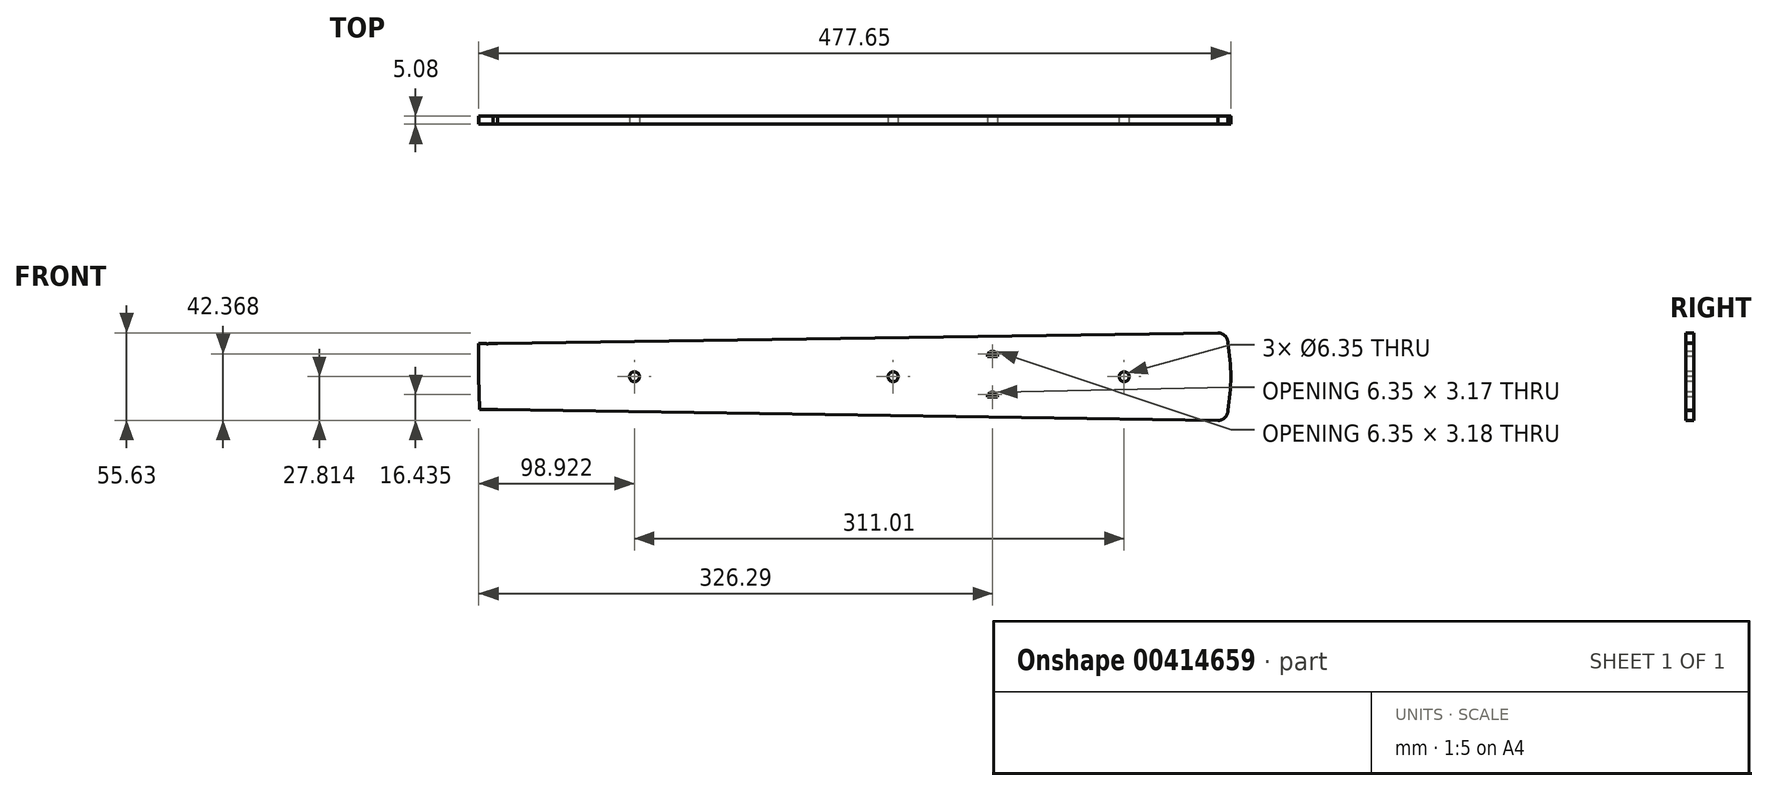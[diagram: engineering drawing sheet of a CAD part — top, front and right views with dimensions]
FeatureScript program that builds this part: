
annotation { "Feature Type Name" : "Feature", "Feature Type Description" : "" }
export const myFeature = defineFeature(function(context is Context, id is Id, definition is map)
    precondition{}
    {
        {
            var Q0;
            Q0=qCreatedBy(makeId("Front.planeOp"),FACE);
            var sketch = newSketch(context, id + "F0", { "sketchPlane" : qUnion([Q0])});
            skLineSegment(sketch, "E0", {"start": v(-164.23, 27.6) * mm, "end": v(293.18, 27.6) * mm});
            skLineSegment(sketch, "E1", {"start": v(-164.23, 48.56) * mm, "end": v(-164.23, 6.65) * mm});
            skLineSegment(sketch, "E2", {"start": v(-164.23, 6.65) * mm, "end": v(293.18, -0.2) * mm});
            skLineSegment(sketch, "E3", {"start": v(293.18, -0.2) * mm, "end": v(293.18, 55.42) * mm});
            skLineSegment(sketch, "E4", {"start": v(293.18, 55.42) * mm, "end": v(-164.23, 48.56) * mm});
            skArc(sketch, "E5", {"start": v(293.18, -0.2) * mm, "mid": v(297.7, 1.67) * mm, "end": v(299.53, 6.2) * mm});
            skArc(sketch, "E6", {"start": v(299.53, 49) * mm, "mid": v(297.7, 53.53) * mm, "end": v(293.18, 55.42) * mm});
            skArc(sketch, "E7", {"start": v(299.53, 6.2) * mm, "mid": v(301.35, 27.6) * mm, "end": v(299.53, 49) * mm});
            skLineSegment(sketch, "E8.MirrorCS", {"start": v(-167.3, 6.65) * mm, "end": v(-167.3, 48.56) * mm});
            skLineSegment(sketch, "E9.MirrorCS", {"start": v(-175.73, 6.7) * mm, "end": v(-167.3, 6.65) * mm});
            skFitSpline(sketch, "E10.MirrorCS", {"points": [v(-167.3, 48.56) * mm, v(-173.6, 48.56) * mm, v(-180.07, 49.1) * mm, v(-184.37, 49.72) * mm, v(-187.7, 50.38) * mm, v(-189.62, 50.86) * mm, v(-191.82, 51.86) * mm, v(-194.74, 53.34) * mm, v(-198.5, 55.52) * mm, v(-201.03, 57.21) * mm, v(-203.1, 58.73) * mm, v(-204.96, 60.23) * mm, v(-206.37, 61.4) * mm, v(-207.64, 62.55) * mm, v(-209.47, 64.33) * mm, v(-210.92, 65.83) * mm, v(-212, 66.98) * mm, v(-213.97, 69.33) * mm, v(-215.82, 71.75) * mm, v(-217.07, 73.74) * mm], "startDerivative": vector(-80.82, -1.68) * mm, "endDerivative": vector(-28.5, 40.15) * mm});
            skLineSegment(sketch, "E11", {"start": v(-167.3, 48.56) * mm, "end": v(-164.23, 48.56) * mm});
            skLineSegment(sketch, "E12", {"start": v(-164.23, 27.6) * mm, "end": v(-176.3, 27.6) * mm});
            skPoint(sketch, "E13", {"position": v(-127.89, 27.6) * mm});
            skPoint(sketch, "E14", {"position": v(-93.57, 27.6) * mm});
            skPoint(sketch, "E15", {"position": v(-61.19, 27.6) * mm});
            skPoint(sketch, "E16", {"position": v(-30.6, 27.6) * mm});
            skLineSegment(sketch, "E17", {"start": v(-127.89, 49.1) * mm, "end": v(-127.89, 6.1) * mm});
            skLineSegment(sketch, "E18", {"start": v(-93.57, 49.62) * mm, "end": v(-93.57, 27.6) * mm});
            skLineSegment(sketch, "E19", {"start": v(-61.19, 5.1) * mm, "end": v(-61.19, 50.1) * mm});
            skLineSegment(sketch, "E20", {"start": v(-30.6, 50.56) * mm, "end": v(-30.6, 4.65) * mm});
            skPoint(sketch, "E21", {"position": v(-1.75, 27.6) * mm});
            skPoint(sketch, "E22", {"position": v(25.48, 27.6) * mm});
            skPoint(sketch, "E23", {"position": v(51.18, 27.6) * mm});
            skPoint(sketch, "E24", {"position": v(75.44, 27.6) * mm});
            skPoint(sketch, "E25", {"position": v(98.35, 27.6) * mm});
            skLineSegment(sketch, "E26", {"start": v(-1.75, 51) * mm, "end": v(-1.75, 27.6) * mm});
            skLineSegment(sketch, "E27", {"start": v(25.48, 51.4) * mm, "end": v(25.48, 27.6) * mm});
            skLineSegment(sketch, "E28", {"start": v(51.18, 51.79) * mm, "end": v(51.18, 3.42) * mm});
            skLineSegment(sketch, "E29", {"start": v(75.44, 52.15) * mm, "end": v(75.44, 3.06) * mm});
            skLineSegment(sketch, "E30", {"start": v(98.35, 52.5) * mm, "end": v(98.35, 2.71) * mm});
            skPoint(sketch, "E31", {"position": v(119.97, 27.6) * mm});
            skPoint(sketch, "E32", {"position": v(140.36, 27.6) * mm});
            skPoint(sketch, "E33", {"position": v(159.62, 27.6) * mm});
            skPoint(sketch, "E34", {"position": v(177.3, 27.6) * mm});
            skPoint(sketch, "E35", {"position": v(194.95, 27.6) * mm});
            skPoint(sketch, "E36", {"position": v(211.15, 27.6) * mm});
            skPoint(sketch, "E37", {"position": v(226.42, 27.6) * mm});
            skLineSegment(sketch, "E38", {"start": v(119.97, 52.82) * mm, "end": v(119.97, 2.39) * mm});
            skLineSegment(sketch, "E39", {"start": v(140.36, 53.13) * mm, "end": v(140.36, 2.08) * mm});
            skLineSegment(sketch, "E40", {"start": v(159.62, 53.41) * mm, "end": v(159.62, 1.8) * mm});
            skLineSegment(sketch, "E41", {"start": v(177.3, 53.68) * mm, "end": v(177.3, 1.53) * mm});
            skLineSegment(sketch, "E42", {"start": v(194.95, 53.94) * mm, "end": v(194.95, 1.26) * mm});
            skPoint(sketch, "E43", {"position": v(240.85, 27.6) * mm});
            skPoint(sketch, "E44", {"position": v(254.46, 27.6) * mm});
            skPoint(sketch, "E45", {"position": v(267.31, 27.6) * mm});
            skPoint(sketch, "E46", {"position": v(279.45, 27.6) * mm});
            skPoint(sketch, "E47", {"position": v(290.9, 27.6) * mm});
            skLineSegment(sketch, "E48", {"start": v(211.15, 54.19) * mm, "end": v(211.15, 1.02) * mm});
            skLineSegment(sketch, "E49", {"start": v(226.42, 54.42) * mm, "end": v(226.42, 0.8) * mm});
            skLineSegment(sketch, "E50", {"start": v(240.85, 0.58) * mm, "end": v(240.85, 54.63) * mm});
            skLineSegment(sketch, "E51", {"start": v(254.46, 54.84) * mm, "end": v(254.46, 0.37) * mm});
            skLineSegment(sketch, "E52", {"start": v(267.31, 0.18) * mm, "end": v(267.31, 55.03) * mm});
            skLineSegment(sketch, "E53", {"start": v(279.45, 55.21) * mm, "end": v(279.45, 0) * mm});
            skLineSegment(sketch, "E54", {"start": v(290.9, 55.38) * mm, "end": v(290.9, -0.17) * mm});
            skCircle(sketch, "E55", {"center": v(-77.38, 27.6) * mm, "radius": 3.18 * mm});
            skCircle(sketch, "E56", {"center": v(-16.18, 27.6) * mm, "radius": 3.18 * mm});
            skCircle(sketch, "E57", {"center": v(38.33, 27.6) * mm, "radius": 3.18 * mm});
            skCircle(sketch, "E58", {"center": v(86.9, 27.6) * mm, "radius": 3.18 * mm});
            skCircle(sketch, "E59", {"center": v(149.99, 14.64) * mm, "radius": 3.18 * mm});
            skCircle(sketch, "E60", {"center": v(149.99, 40.57) * mm, "radius": 3.18 * mm});
            skCircle(sketch, "E61", {"center": v(203.05, 27.6) * mm, "radius": 3.18 * mm});
            skCircle(sketch, "E62", {"center": v(233.63, 27.6) * mm, "radius": 3.18 * mm});
            skCircle(sketch, "E63", {"center": v(260.89, 27.6) * mm, "radius": 3.18 * mm});
            skCircle(sketch, "E64", {"center": v(285.18, 27.6) * mm, "radius": 3.18 * mm});
            skPoint(sketch, "E65", {"position": v(149.99, 27.6) * mm});
            skLineSegment(sketch, "E66", {"start": v(149.99, 53.27) * mm, "end": v(149.99, 1.94) * mm});
            skLineSegment(sketch, "E67", {"start": v(140.36, 14.64) * mm, "end": v(159.62, 14.64) * mm});
            skLineSegment(sketch, "E68", {"start": v(140.36, 40.57) * mm, "end": v(159.62, 40.57) * mm});
            skLineSegment(sketch, "E69", {"start": v(-167.3, 6.65) * mm, "end": v(-164.23, 6.65) * mm});
            skLineSegment(sketch, "E70", {"start": v(-1.75, 4.21) * mm, "end": v(-1.75, 27.6) * mm});
            skLineSegment(sketch, "E71", {"start": v(25.48, 27.6) * mm, "end": v(25.48, 3.8) * mm});
            skLineSegment(sketch, "E72", {"start": v(-93.57, 27.6) * mm, "end": v(-93.57, 5.59) * mm});
            skPoint(sketch, "E73", {"position": v(-176.3, 27.6) * mm});
            skLineSegment(sketch, "E74", {"start": v(-176.3, 27.6) * mm, "end": v(-175.73, 6.7) * mm});
            skLineSegment(sketch, "E75", {"start": v(-176.3, 27.6) * mm, "end": v(-176.3, 48.72) * mm});
            skPoint(sketch, "E76.start.orphan", {"position": v(-192.8, 27.6) * mm});
            skSolve(sketch);
        }
        {
            var Q0;
            {var subQ0=sQuery(id+"F0.wireOp",EDGE,"E42");var subQ3=sQuery(id+"F0.wireOp",EDGE,"E0");var subQ4=makeQuery(id+"F0.imprint","INTERSECT",VERTEX,{"derivedFrom":[subQ3,subQ0]});Q0=makeQuery(id+"F0.imprint","IMPRINT",FACE,{"disambiguationData":[TD([[makeQuery(id+"F0.imprint","IMPRINT",EDGE,{"disambiguationData":[TD([[subQ4,-1.0]])],"derivedFrom":subQ3}),1.0]])]});}
            var Q1;
            {var subQ5=sQuery(id+"F0.wireOp",EDGE,"E71");Q1=makeQuery(id+"F0.imprint","IMPRINT",FACE,{"disambiguationData":[TD([[makeQuery(id+"F0.imprint","IMPRINT",EDGE,{"derivedFrom":subQ5}),1.0]])]});}
            var Q2;
            {var subQ0=sQuery(id+"F0.wireOp",EDGE,"E28");var subQ1=sQuery(id+"F0.wireOp",EDGE,"E0");var subQ2=makeQuery(id+"F0.imprint","INTERSECT",VERTEX,{"derivedFrom":[subQ1,subQ0]});Q2=makeQuery(id+"F0.imprint","IMPRINT",FACE,{"disambiguationData":[TD([[makeQuery(id+"F0.imprint","IMPRINT",EDGE,{"disambiguationData":[TD([[subQ2,-1.0]])],"derivedFrom":subQ1}),1.0]])]});}
            var Q3;
            {var subQ0=sQuery(id+"F0.wireOp",EDGE,"E30");var subQ1=sQuery(id+"F0.wireOp",EDGE,"E0");var subQ2=makeQuery(id+"F0.imprint","INTERSECT",VERTEX,{"derivedFrom":[subQ1,subQ0]});Q3=makeQuery(id+"F0.imprint","IMPRINT",FACE,{"disambiguationData":[TD([[makeQuery(id+"F0.imprint","IMPRINT",EDGE,{"disambiguationData":[TD([[subQ2,-1.0]])],"derivedFrom":subQ1}),1.0]])]});}
            var Q4;
            {var subQ0=sQuery(id+"F0.wireOp",EDGE,"E72");Q4=makeQuery(id+"F0.imprint","IMPRINT",FACE,{"disambiguationData":[TD([[makeQuery(id+"F0.imprint","IMPRINT",EDGE,{"derivedFrom":subQ0}),-1.0]])]});}
            var Q5;
            {var subQ5=sQuery(id+"F0.wireOp",EDGE,"E26");Q5=makeQuery(id+"F0.imprint","IMPRINT",FACE,{"disambiguationData":[TD([[makeQuery(id+"F0.imprint","IMPRINT",EDGE,{"derivedFrom":subQ5}),-1.0]])]});}
            var Q6;
            {var subQ0=sQuery(id+"F0.wireOp",EDGE,"E18");Q6=makeQuery(id+"F0.imprint","IMPRINT",FACE,{"disambiguationData":[TD([[makeQuery(id+"F0.imprint","IMPRINT",EDGE,{"derivedFrom":subQ0}),-1.0]])]});}
            var Q7;
            {var subQ0=sQuery(id+"F0.wireOp",EDGE,"E19");var subQ1=sQuery(id+"F0.wireOp",EDGE,"E0");var subQ2=makeQuery(id+"F0.imprint","INTERSECT",VERTEX,{"derivedFrom":[subQ1,subQ0]});Q7=makeQuery(id+"F0.imprint","IMPRINT",FACE,{"disambiguationData":[TD([[makeQuery(id+"F0.imprint","IMPRINT",EDGE,{"disambiguationData":[TD([[subQ2,-1.0]])],"derivedFrom":subQ1}),-1.0]])]});}
            var Q8;
            {var subQ0=sQuery(id+"F0.wireOp",EDGE,"E28");var subQ1=sQuery(id+"F0.wireOp",EDGE,"E0");var subQ2=makeQuery(id+"F0.imprint","INTERSECT",VERTEX,{"derivedFrom":[subQ1,subQ0]});Q8=makeQuery(id+"F0.imprint","IMPRINT",FACE,{"disambiguationData":[TD([[makeQuery(id+"F0.imprint","IMPRINT",EDGE,{"disambiguationData":[TD([[subQ2,-1.0]])],"derivedFrom":subQ1}),-1.0]])]});}
            var Q9;
            Q9=makeQuery(id+"F0.imprint","IMPRINT",FACE,{"disambiguationData":[TD([[makeQuery(id+"F0.imprint","IMPRINT",EDGE,{"derivedFrom":sQuery(id+"F0.wireOp",EDGE,"d4d94dd8-df4f-4db1-98d0-309e30baff10.MirrorCS")}),-1.0]])]});
            var Q10;
            {var subQ0=sQuery(id+"F0.wireOp",EDGE,"E38");var subQ3=sQuery(id+"F0.wireOp",EDGE,"E0");var subQ4=makeQuery(id+"F0.imprint","INTERSECT",VERTEX,{"derivedFrom":[subQ3,subQ0]});Q10=makeQuery(id+"F0.imprint","IMPRINT",FACE,{"disambiguationData":[TD([[makeQuery(id+"F0.imprint","IMPRINT",EDGE,{"disambiguationData":[TD([[subQ4,-1.0]])],"derivedFrom":subQ3}),-1.0]])]});}
            var Q11;
            {var subQ0=sQuery(id+"F0.wireOp",EDGE,"E30");var subQ1=sQuery(id+"F0.wireOp",EDGE,"E0");var subQ2=makeQuery(id+"F0.imprint","INTERSECT",VERTEX,{"derivedFrom":[subQ1,subQ0]});Q11=makeQuery(id+"F0.imprint","IMPRINT",FACE,{"disambiguationData":[TD([[makeQuery(id+"F0.imprint","IMPRINT",EDGE,{"disambiguationData":[TD([[subQ2,-1.0]])],"derivedFrom":subQ1}),-1.0]])]});}
            var Q12;
            {var subQ0=sQuery(id+"F0.wireOp",EDGE,"E18");Q12=makeQuery(id+"F0.imprint","IMPRINT",FACE,{"disambiguationData":[TD([[makeQuery(id+"F0.imprint","IMPRINT",EDGE,{"derivedFrom":subQ0}),1.0]])]});}
            var Q13;
            {var subQ0=sQuery(id+"F0.wireOp",EDGE,"E27");Q13=makeQuery(id+"F0.imprint","IMPRINT",FACE,{"disambiguationData":[TD([[makeQuery(id+"F0.imprint","IMPRINT",EDGE,{"derivedFrom":subQ0}),1.0]])]});}
            var Q14;
            {var subQ0=sQuery(id+"F0.wireOp",EDGE,"E19");var subQ1=sQuery(id+"F0.wireOp",EDGE,"E0");var subQ2=makeQuery(id+"F0.imprint","INTERSECT",VERTEX,{"derivedFrom":[subQ1,subQ0]});Q14=makeQuery(id+"F0.imprint","IMPRINT",FACE,{"disambiguationData":[TD([[makeQuery(id+"F0.imprint","IMPRINT",EDGE,{"disambiguationData":[TD([[subQ2,-1.0]])],"derivedFrom":subQ1}),1.0]])]});}
            var Q15;
            {var subQ3=sQuery(id+"F0.wireOp",EDGE,"E17");var subQ5=sQuery(id+"F0.wireOp",EDGE,"E2");var subQ7=makeQuery(id+"F0.imprint","INTERSECT",VERTEX,{"derivedFrom":[subQ5,subQ3]});Q15=makeQuery(id+"F0.imprint","IMPRINT",FACE,{"disambiguationData":[TD([[makeQuery(id+"F0.imprint","IMPRINT",EDGE,{"disambiguationData":[TD([[subQ7,1.0]])],"derivedFrom":subQ3}),-1.0]])]});}
            var Q16;
            {var subQ0=sQuery(id+"F0.wireOp",EDGE,"E10.MirrorCS");Q16=makeQuery(id+"F0.imprint","IMPRINT",FACE,{"disambiguationData":[TD([[makeQuery(id+"F0.imprint","IMPRINT",EDGE,{"derivedFrom":subQ0}),1.0]])]});}
            var Q17;
            {var subQ0=sQuery(id+"F0.wireOp",EDGE,"E29");var subQ3=sQuery(id+"F0.wireOp",EDGE,"E0");var subQ4=makeQuery(id+"F0.imprint","INTERSECT",VERTEX,{"derivedFrom":[subQ3,subQ0]});Q17=makeQuery(id+"F0.imprint","IMPRINT",FACE,{"disambiguationData":[TD([[makeQuery(id+"F0.imprint","IMPRINT",EDGE,{"disambiguationData":[TD([[subQ4,-1.0]])],"derivedFrom":subQ3}),-1.0]])]});}
            var Q18;
            {var subQ0=sQuery(id+"F0.wireOp",EDGE,"E41");var subQ1=sQuery(id+"F0.wireOp",EDGE,"E0");var subQ2=makeQuery(id+"F0.imprint","INTERSECT",VERTEX,{"derivedFrom":[subQ1,subQ0]});Q18=makeQuery(id+"F0.imprint","IMPRINT",FACE,{"disambiguationData":[TD([[makeQuery(id+"F0.imprint","IMPRINT",EDGE,{"disambiguationData":[TD([[subQ2,-1.0]])],"derivedFrom":subQ1}),-1.0]])]});}
            var Q19;
            {var subQ0=sQuery(id+"F0.wireOp",EDGE,"E29");var subQ3=sQuery(id+"F0.wireOp",EDGE,"E0");var subQ4=makeQuery(id+"F0.imprint","INTERSECT",VERTEX,{"derivedFrom":[subQ3,subQ0]});Q19=makeQuery(id+"F0.imprint","IMPRINT",FACE,{"disambiguationData":[TD([[makeQuery(id+"F0.imprint","IMPRINT",EDGE,{"disambiguationData":[TD([[subQ4,-1.0]])],"derivedFrom":subQ3}),1.0]])]});}
            var Q20;
            {var subQ0=sQuery(id+"F0.wireOp",EDGE,"E42");var subQ3=sQuery(id+"F0.wireOp",EDGE,"E0");var subQ4=makeQuery(id+"F0.imprint","INTERSECT",VERTEX,{"derivedFrom":[subQ3,subQ0]});Q20=makeQuery(id+"F0.imprint","IMPRINT",FACE,{"disambiguationData":[TD([[makeQuery(id+"F0.imprint","IMPRINT",EDGE,{"disambiguationData":[TD([[subQ4,-1.0]])],"derivedFrom":subQ3}),-1.0]])]});}
            var Q21;
            {var subQ3=sQuery(id+"F0.wireOp",EDGE,"E17");var subQ5=sQuery(id+"F0.wireOp",EDGE,"E4");var subQ7=makeQuery(id+"F0.imprint","INTERSECT",VERTEX,{"derivedFrom":[subQ5,subQ3]});Q21=makeQuery(id+"F0.imprint","IMPRINT",FACE,{"disambiguationData":[TD([[makeQuery(id+"F0.imprint","IMPRINT",EDGE,{"disambiguationData":[TD([[subQ7,-1.0]])],"derivedFrom":subQ3}),-1.0]])]});}
            var Q22;
            {var subQ4=sQuery(id+"F0.wireOp",EDGE,"E38");var subQ6=sQuery(id+"F0.wireOp",EDGE,"E0");var subQ7=makeQuery(id+"F0.imprint","INTERSECT",VERTEX,{"derivedFrom":[subQ6,subQ4]});Q22=makeQuery(id+"F0.imprint","IMPRINT",FACE,{"disambiguationData":[TD([[makeQuery(id+"F0.imprint","IMPRINT",EDGE,{"disambiguationData":[TD([[subQ7,-1.0]])],"derivedFrom":subQ6}),1.0]])]});}
            var Q23;
            {var subQ5=sQuery(id+"F0.wireOp",EDGE,"E70");Q23=makeQuery(id+"F0.imprint","IMPRINT",FACE,{"disambiguationData":[TD([[makeQuery(id+"F0.imprint","IMPRINT",EDGE,{"derivedFrom":subQ5}),1.0]])]});}
            var Q24;
            {var subQ0=sQuery(id+"F0.wireOp",EDGE,"E52");var subQ1=sQuery(id+"F0.wireOp",EDGE,"E0");var subQ2=makeQuery(id+"F0.imprint","INTERSECT",VERTEX,{"derivedFrom":[subQ1,subQ0]});Q24=makeQuery(id+"F0.imprint","IMPRINT",FACE,{"disambiguationData":[TD([[makeQuery(id+"F0.imprint","IMPRINT",EDGE,{"disambiguationData":[TD([[subQ2,-1.0]])],"derivedFrom":subQ1}),-1.0]])]});}
            var Q25;
            {var subQ0=sQuery(id+"F0.wireOp",EDGE,"E41");var subQ1=sQuery(id+"F0.wireOp",EDGE,"E0");var subQ2=makeQuery(id+"F0.imprint","INTERSECT",VERTEX,{"derivedFrom":[subQ1,subQ0]});Q25=makeQuery(id+"F0.imprint","IMPRINT",FACE,{"disambiguationData":[TD([[makeQuery(id+"F0.imprint","IMPRINT",EDGE,{"disambiguationData":[TD([[subQ2,-1.0]])],"derivedFrom":subQ1}),1.0]])]});}
            var Q26;
            {var subQ0=sQuery(id+"F0.wireOp",EDGE,"E53");var subQ3=sQuery(id+"F0.wireOp",EDGE,"E0");var subQ4=makeQuery(id+"F0.imprint","INTERSECT",VERTEX,{"derivedFrom":[subQ3,subQ0]});Q26=makeQuery(id+"F0.imprint","IMPRINT",FACE,{"disambiguationData":[TD([[makeQuery(id+"F0.imprint","IMPRINT",EDGE,{"disambiguationData":[TD([[subQ4,-1.0]])],"derivedFrom":subQ3}),1.0]])]});}
            var Q27;
            {var subQ0=sQuery(id+"F0.wireOp",EDGE,"E52");var subQ1=sQuery(id+"F0.wireOp",EDGE,"E0");var subQ2=makeQuery(id+"F0.imprint","INTERSECT",VERTEX,{"derivedFrom":[subQ1,subQ0]});Q27=makeQuery(id+"F0.imprint","IMPRINT",FACE,{"disambiguationData":[TD([[makeQuery(id+"F0.imprint","IMPRINT",EDGE,{"disambiguationData":[TD([[subQ2,-1.0]])],"derivedFrom":subQ1}),1.0]])]});}
            var Q28;
            {var subQ0=sQuery(id+"F0.wireOp",EDGE,"E40");var subQ6=sQuery(id+"F0.wireOp",EDGE,"E0");var subQ7=makeQuery(id+"F0.imprint","INTERSECT",VERTEX,{"derivedFrom":[subQ6,subQ0]});Q28=makeQuery(id+"F0.imprint","IMPRINT",FACE,{"disambiguationData":[TD([[makeQuery(id+"F0.imprint","IMPRINT",EDGE,{"disambiguationData":[TD([[subQ7,-1.0]])],"derivedFrom":subQ6}),1.0]])]});}
            var Q29;
            {var subQ1=sQuery(id+"F0.wireOp",EDGE,"E2");var subQ5=sQuery(id+"F0.wireOp",EDGE,"E39");var subQ6=makeQuery(id+"F0.imprint","INTERSECT",VERTEX,{"derivedFrom":[subQ1,subQ5]});Q29=makeQuery(id+"F0.imprint","IMPRINT",FACE,{"disambiguationData":[TD([[makeQuery(id+"F0.imprint","IMPRINT",EDGE,{"disambiguationData":[TD([[subQ6,-1.0]])],"derivedFrom":subQ1}),1.0]])]});}
            var Q30;
            {var subQ0=sQuery(id+"F0.wireOp",EDGE,"E49");var subQ3=sQuery(id+"F0.wireOp",EDGE,"E0");var subQ4=makeQuery(id+"F0.imprint","INTERSECT",VERTEX,{"derivedFrom":[subQ3,subQ0]});Q30=makeQuery(id+"F0.imprint","IMPRINT",FACE,{"disambiguationData":[TD([[makeQuery(id+"F0.imprint","IMPRINT",EDGE,{"disambiguationData":[TD([[subQ4,-1.0]])],"derivedFrom":subQ3}),-1.0]])]});}
            var Q31;
            {var subQ0=sQuery(id+"F0.wireOp",EDGE,"E48");var subQ1=sQuery(id+"F0.wireOp",EDGE,"E0");var subQ2=makeQuery(id+"F0.imprint","INTERSECT",VERTEX,{"derivedFrom":[subQ1,subQ0]});Q31=makeQuery(id+"F0.imprint","IMPRINT",FACE,{"disambiguationData":[TD([[makeQuery(id+"F0.imprint","IMPRINT",EDGE,{"disambiguationData":[TD([[subQ2,-1.0]])],"derivedFrom":subQ1}),-1.0]])]});}
            var Q32;
            {var subQ0=sQuery(id+"F0.wireOp",EDGE,"E50");var subQ1=sQuery(id+"F0.wireOp",EDGE,"E0");var subQ2=makeQuery(id+"F0.imprint","INTERSECT",VERTEX,{"derivedFrom":[subQ1,subQ0]});Q32=makeQuery(id+"F0.imprint","IMPRINT",FACE,{"disambiguationData":[TD([[makeQuery(id+"F0.imprint","IMPRINT",EDGE,{"disambiguationData":[TD([[subQ2,-1.0]])],"derivedFrom":subQ1}),1.0]])]});}
            var Q33;
            {var subQ0=sQuery(id+"F0.wireOp",EDGE,"E40");var subQ4=sQuery(id+"F0.wireOp",EDGE,"E0");var subQ5=makeQuery(id+"F0.imprint","INTERSECT",VERTEX,{"derivedFrom":[subQ4,subQ0]});Q33=makeQuery(id+"F0.imprint","IMPRINT",FACE,{"disambiguationData":[TD([[makeQuery(id+"F0.imprint","IMPRINT",EDGE,{"disambiguationData":[TD([[subQ5,-1.0]])],"derivedFrom":subQ4}),-1.0]])]});}
            var Q34;
            {var subQ0=sQuery(id+"F0.wireOp",EDGE,"E51");var subQ3=sQuery(id+"F0.wireOp",EDGE,"E0");var subQ4=makeQuery(id+"F0.imprint","INTERSECT",VERTEX,{"derivedFrom":[subQ3,subQ0]});Q34=makeQuery(id+"F0.imprint","IMPRINT",FACE,{"disambiguationData":[TD([[makeQuery(id+"F0.imprint","IMPRINT",EDGE,{"disambiguationData":[TD([[subQ4,-1.0]])],"derivedFrom":subQ3}),1.0]])]});}
            var Q35;
            {var subQ5=sQuery(id+"F0.wireOp",EDGE,"E4");var subQ7=sQuery(id+"F0.wireOp",EDGE,"E39");var subQ8=makeQuery(id+"F0.imprint","INTERSECT",VERTEX,{"derivedFrom":[subQ5,subQ7]});Q35=makeQuery(id+"F0.imprint","IMPRINT",FACE,{"disambiguationData":[TD([[makeQuery(id+"F0.imprint","IMPRINT",EDGE,{"disambiguationData":[TD([[subQ8,1.0]])],"derivedFrom":subQ5}),1.0]])]});}
            var Q36;
            {var subQ0=sQuery(id+"F0.wireOp",EDGE,"E49");var subQ3=sQuery(id+"F0.wireOp",EDGE,"E0");var subQ4=makeQuery(id+"F0.imprint","INTERSECT",VERTEX,{"derivedFrom":[subQ3,subQ0]});Q36=makeQuery(id+"F0.imprint","IMPRINT",FACE,{"disambiguationData":[TD([[makeQuery(id+"F0.imprint","IMPRINT",EDGE,{"disambiguationData":[TD([[subQ4,-1.0]])],"derivedFrom":subQ3}),1.0]])]});}
            var Q37;
            {var subQ0=sQuery(id+"F0.wireOp",EDGE,"E48");var subQ1=sQuery(id+"F0.wireOp",EDGE,"E0");var subQ2=makeQuery(id+"F0.imprint","INTERSECT",VERTEX,{"derivedFrom":[subQ1,subQ0]});Q37=makeQuery(id+"F0.imprint","IMPRINT",FACE,{"disambiguationData":[TD([[makeQuery(id+"F0.imprint","IMPRINT",EDGE,{"disambiguationData":[TD([[subQ2,-1.0]])],"derivedFrom":subQ1}),1.0]])]});}
            var Q38;
            {var subQ0=sQuery(id+"F0.wireOp",EDGE,"E26");Q38=makeQuery(id+"F0.imprint","IMPRINT",FACE,{"disambiguationData":[TD([[makeQuery(id+"F0.imprint","IMPRINT",EDGE,{"derivedFrom":subQ0}),1.0]])]});}
            var Q39;
            {var subQ0=sQuery(id+"F0.wireOp",EDGE,"E70");Q39=makeQuery(id+"F0.imprint","IMPRINT",FACE,{"disambiguationData":[TD([[makeQuery(id+"F0.imprint","IMPRINT",EDGE,{"derivedFrom":subQ0}),-1.0]])]});}
            var Q40;
            {var subQ0=sQuery(id+"F0.wireOp",EDGE,"E50");var subQ1=sQuery(id+"F0.wireOp",EDGE,"E0");var subQ2=makeQuery(id+"F0.imprint","INTERSECT",VERTEX,{"derivedFrom":[subQ1,subQ0]});Q40=makeQuery(id+"F0.imprint","IMPRINT",FACE,{"disambiguationData":[TD([[makeQuery(id+"F0.imprint","IMPRINT",EDGE,{"disambiguationData":[TD([[subQ2,-1.0]])],"derivedFrom":subQ1}),-1.0]])]});}
            var Q41;
            {var subQ3=sQuery(id+"F0.wireOp",EDGE,"E72");Q41=makeQuery(id+"F0.imprint","IMPRINT",FACE,{"disambiguationData":[TD([[makeQuery(id+"F0.imprint","IMPRINT",EDGE,{"derivedFrom":subQ3}),1.0]])]});}
            var Q42;
            {var subQ0=sQuery(id+"F0.wireOp",EDGE,"E51");var subQ3=sQuery(id+"F0.wireOp",EDGE,"E0");var subQ4=makeQuery(id+"F0.imprint","INTERSECT",VERTEX,{"derivedFrom":[subQ3,subQ0]});Q42=makeQuery(id+"F0.imprint","IMPRINT",FACE,{"disambiguationData":[TD([[makeQuery(id+"F0.imprint","IMPRINT",EDGE,{"disambiguationData":[TD([[subQ4,-1.0]])],"derivedFrom":subQ3}),-1.0]])]});}
            var Q43;
            {var subQ0=sQuery(id+"F0.wireOp",EDGE,"E57");var subQ1=sQuery(id+"F0.wireOp",EDGE,"E0");var subQ2=makeQuery(id+"F0.imprint","INTERSECT",VERTEX,{"disambiguationData":[OD(0.0)],"derivedFrom":[subQ1,subQ0]});Q43=makeQuery(id+"F0.imprint","IMPRINT",FACE,{"disambiguationData":[TD([[makeQuery(id+"F0.imprint","IMPRINT",EDGE,{"disambiguationData":[TD([[subQ2,-1.0]])],"derivedFrom":subQ1}),1.0]])]});}
            var Q44;
            {var subQ0=sQuery(id+"F0.wireOp",EDGE,"E57");var subQ1=sQuery(id+"F0.wireOp",EDGE,"E0");var subQ2=makeQuery(id+"F0.imprint","INTERSECT",VERTEX,{"disambiguationData":[OD(0.0)],"derivedFrom":[subQ1,subQ0]});Q44=makeQuery(id+"F0.imprint","IMPRINT",FACE,{"disambiguationData":[TD([[makeQuery(id+"F0.imprint","IMPRINT",EDGE,{"disambiguationData":[TD([[subQ2,-1.0]])],"derivedFrom":subQ1}),-1.0]])]});}
            var Q45;
            {var subQ0=sQuery(id+"F0.wireOp",EDGE,"E58");var subQ1=sQuery(id+"F0.wireOp",EDGE,"E0");var subQ2=makeQuery(id+"F0.imprint","INTERSECT",VERTEX,{"disambiguationData":[OD(0.0)],"derivedFrom":[subQ1,subQ0]});Q45=makeQuery(id+"F0.imprint","IMPRINT",FACE,{"disambiguationData":[TD([[makeQuery(id+"F0.imprint","IMPRINT",EDGE,{"disambiguationData":[TD([[subQ2,-1.0]])],"derivedFrom":subQ1}),1.0]])]});}
            var Q46;
            {var subQ1=sQuery(id+"F0.wireOp",EDGE,"E0");var subQ7=sQuery(id+"F0.wireOp",EDGE,"E39");var subQ9=makeQuery(id+"F0.imprint","INTERSECT",VERTEX,{"derivedFrom":[subQ1,subQ7]});Q46=makeQuery(id+"F0.imprint","IMPRINT",FACE,{"disambiguationData":[TD([[makeQuery(id+"F0.imprint","IMPRINT",EDGE,{"disambiguationData":[TD([[subQ9,-1.0]])],"derivedFrom":subQ1}),-1.0]])]});}
            var Q47;
            {var subQ0=sQuery(id+"F0.wireOp",EDGE,"E55");var subQ1=sQuery(id+"F0.wireOp",EDGE,"E0");var subQ2=makeQuery(id+"F0.imprint","INTERSECT",VERTEX,{"disambiguationData":[OD(0.0)],"derivedFrom":[subQ1,subQ0]});Q47=makeQuery(id+"F0.imprint","IMPRINT",FACE,{"disambiguationData":[TD([[makeQuery(id+"F0.imprint","IMPRINT",EDGE,{"disambiguationData":[TD([[subQ2,-1.0]])],"derivedFrom":subQ1}),1.0]])]});}
            var Q48;
            {var subQ0=sQuery(id+"F0.wireOp",EDGE,"E55");var subQ1=sQuery(id+"F0.wireOp",EDGE,"E0");var subQ2=makeQuery(id+"F0.imprint","INTERSECT",VERTEX,{"disambiguationData":[OD(0.0)],"derivedFrom":[subQ1,subQ0]});Q48=makeQuery(id+"F0.imprint","IMPRINT",FACE,{"disambiguationData":[TD([[makeQuery(id+"F0.imprint","IMPRINT",EDGE,{"disambiguationData":[TD([[subQ2,-1.0]])],"derivedFrom":subQ1}),-1.0]])]});}
            var Q49;
            {var subQ0=sQuery(id+"F0.wireOp",EDGE,"E56");var subQ1=sQuery(id+"F0.wireOp",EDGE,"E0");var subQ2=makeQuery(id+"F0.imprint","INTERSECT",VERTEX,{"disambiguationData":[OD(0.0)],"derivedFrom":[subQ1,subQ0]});Q49=makeQuery(id+"F0.imprint","IMPRINT",FACE,{"disambiguationData":[TD([[makeQuery(id+"F0.imprint","IMPRINT",EDGE,{"disambiguationData":[TD([[subQ2,-1.0]])],"derivedFrom":subQ1}),1.0]])]});}
            var Q50;
            {var subQ0=sQuery(id+"F0.wireOp",EDGE,"E56");var subQ1=sQuery(id+"F0.wireOp",EDGE,"E0");var subQ2=makeQuery(id+"F0.imprint","INTERSECT",VERTEX,{"disambiguationData":[OD(0.0)],"derivedFrom":[subQ1,subQ0]});Q50=makeQuery(id+"F0.imprint","IMPRINT",FACE,{"disambiguationData":[TD([[makeQuery(id+"F0.imprint","IMPRINT",EDGE,{"disambiguationData":[TD([[subQ2,-1.0]])],"derivedFrom":subQ1}),-1.0]])]});}
            var Q51;
            {var subQ0=sQuery(id+"F0.wireOp",EDGE,"E58");var subQ1=sQuery(id+"F0.wireOp",EDGE,"E0");var subQ2=makeQuery(id+"F0.imprint","INTERSECT",VERTEX,{"disambiguationData":[OD(0.0)],"derivedFrom":[subQ1,subQ0]});Q51=makeQuery(id+"F0.imprint","IMPRINT",FACE,{"disambiguationData":[TD([[makeQuery(id+"F0.imprint","IMPRINT",EDGE,{"disambiguationData":[TD([[subQ2,-1.0]])],"derivedFrom":subQ1}),-1.0]])]});}
            var Q52;
            {var subQ0=sQuery(id+"F0.wireOp",EDGE,"E53");var subQ3=sQuery(id+"F0.wireOp",EDGE,"E0");var subQ4=makeQuery(id+"F0.imprint","INTERSECT",VERTEX,{"derivedFrom":[subQ3,subQ0]});Q52=makeQuery(id+"F0.imprint","IMPRINT",FACE,{"disambiguationData":[TD([[makeQuery(id+"F0.imprint","IMPRINT",EDGE,{"disambiguationData":[TD([[subQ4,-1.0]])],"derivedFrom":subQ3}),-1.0]])]});}
            var Q53;
            {var subQ3=sQuery(id+"F0.wireOp",EDGE,"E0");var subQ7=sQuery(id+"F0.wireOp",EDGE,"E66");var subQ8=makeQuery(id+"F0.imprint","INTERSECT",VERTEX,{"derivedFrom":[subQ3,subQ7]});Q53=makeQuery(id+"F0.imprint","IMPRINT",FACE,{"disambiguationData":[TD([[makeQuery(id+"F0.imprint","IMPRINT",EDGE,{"disambiguationData":[TD([[subQ8,-1.0]])],"derivedFrom":subQ3}),-1.0]])]});}
            var Q54;
            {var subQ3=sQuery(id+"F0.wireOp",EDGE,"E5");Q54=makeQuery(id+"F0.imprint","IMPRINT",FACE,{"disambiguationData":[TD([[makeQuery(id+"F0.imprint","IMPRINT",EDGE,{"derivedFrom":subQ3}),1.0]])]});}
            var Q55;
            {var subQ5=sQuery(id+"F0.wireOp",EDGE,"E39");var subQ7=sQuery(id+"F0.wireOp",EDGE,"E0");var subQ8=makeQuery(id+"F0.imprint","INTERSECT",VERTEX,{"derivedFrom":[subQ7,subQ5]});Q55=makeQuery(id+"F0.imprint","IMPRINT",FACE,{"disambiguationData":[TD([[makeQuery(id+"F0.imprint","IMPRINT",EDGE,{"disambiguationData":[TD([[subQ8,-1.0]])],"derivedFrom":subQ7}),1.0]])]});}
            var Q56;
            {var subQ0=sQuery(id+"F0.wireOp",EDGE,"E66");var subQ1=sQuery(id+"F0.wireOp",EDGE,"E0");var subQ2=makeQuery(id+"F0.imprint","INTERSECT",VERTEX,{"derivedFrom":[subQ1,subQ0]});Q56=makeQuery(id+"F0.imprint","IMPRINT",FACE,{"disambiguationData":[TD([[makeQuery(id+"F0.imprint","IMPRINT",EDGE,{"disambiguationData":[TD([[subQ2,-1.0]])],"derivedFrom":subQ1}),1.0]])]});}
            var Q57;
            {var subQ1=sQuery(id+"F0.wireOp",EDGE,"E2");var subQ7=sQuery(id+"F0.wireOp",EDGE,"E40");var subQ8=makeQuery(id+"F0.imprint","INTERSECT",VERTEX,{"derivedFrom":[subQ1,subQ7]});Q57=makeQuery(id+"F0.imprint","IMPRINT",FACE,{"disambiguationData":[TD([[makeQuery(id+"F0.imprint","IMPRINT",EDGE,{"disambiguationData":[TD([[subQ8,1.0]])],"derivedFrom":subQ1}),1.0]])]});}
            var Q58;
            {var subQ5=sQuery(id+"F0.wireOp",EDGE,"E40");var subQ6=sQuery(id+"F0.wireOp",EDGE,"E4");var subQ7=makeQuery(id+"F0.imprint","INTERSECT",VERTEX,{"derivedFrom":[subQ6,subQ5]});Q58=makeQuery(id+"F0.imprint","IMPRINT",FACE,{"disambiguationData":[TD([[makeQuery(id+"F0.imprint","IMPRINT",EDGE,{"disambiguationData":[TD([[subQ7,-1.0]])],"derivedFrom":subQ6}),1.0]])]});}
            var Q59;
            {var subQ0=sQuery(id+"F0.wireOp",EDGE,"E66");var subQ1=sQuery(id+"F0.wireOp",EDGE,"E59");var subQ2=makeQuery(id+"F0.imprint","INTERSECT",VERTEX,{"disambiguationData":[OD(0.0)],"derivedFrom":[subQ1,subQ0]});Q59=makeQuery(id+"F0.imprint","IMPRINT",FACE,{"disambiguationData":[TD([[makeQuery(id+"F0.imprint","IMPRINT",EDGE,{"disambiguationData":[TD([[subQ2,-1.0]])],"derivedFrom":subQ1}),1.0]])]});}
            var Q60;
            {var subQ0=sQuery(id+"F0.wireOp",EDGE,"E66");var subQ1=sQuery(id+"F0.wireOp",EDGE,"E60");var subQ2=makeQuery(id+"F0.imprint","INTERSECT",VERTEX,{"disambiguationData":[OD(0.0)],"derivedFrom":[subQ1,subQ0]});Q60=makeQuery(id+"F0.imprint","IMPRINT",FACE,{"disambiguationData":[TD([[makeQuery(id+"F0.imprint","IMPRINT",EDGE,{"disambiguationData":[TD([[subQ2,-1.0]])],"derivedFrom":subQ1}),1.0]])]});}
            var Q61;
            {var subQ0=sQuery(id+"F0.wireOp",EDGE,"E61");var subQ1=sQuery(id+"F0.wireOp",EDGE,"E0");var subQ2=makeQuery(id+"F0.imprint","INTERSECT",VERTEX,{"disambiguationData":[OD(0.0)],"derivedFrom":[subQ1,subQ0]});Q61=makeQuery(id+"F0.imprint","IMPRINT",FACE,{"disambiguationData":[TD([[makeQuery(id+"F0.imprint","IMPRINT",EDGE,{"disambiguationData":[TD([[subQ2,-1.0]])],"derivedFrom":subQ1}),-1.0]])]});}
            var Q62;
            {var subQ0=sQuery(id+"F0.wireOp",EDGE,"E61");var subQ1=sQuery(id+"F0.wireOp",EDGE,"E0");var subQ2=makeQuery(id+"F0.imprint","INTERSECT",VERTEX,{"disambiguationData":[OD(0.0)],"derivedFrom":[subQ1,subQ0]});Q62=makeQuery(id+"F0.imprint","IMPRINT",FACE,{"disambiguationData":[TD([[makeQuery(id+"F0.imprint","IMPRINT",EDGE,{"disambiguationData":[TD([[subQ2,-1.0]])],"derivedFrom":subQ1}),1.0]])]});}
            var Q63;
            {var subQ0=sQuery(id+"F0.wireOp",EDGE,"E62");var subQ1=sQuery(id+"F0.wireOp",EDGE,"E0");var subQ2=makeQuery(id+"F0.imprint","INTERSECT",VERTEX,{"disambiguationData":[OD(0.0)],"derivedFrom":[subQ1,subQ0]});Q63=makeQuery(id+"F0.imprint","IMPRINT",FACE,{"disambiguationData":[TD([[makeQuery(id+"F0.imprint","IMPRINT",EDGE,{"disambiguationData":[TD([[subQ2,-1.0]])],"derivedFrom":subQ1}),1.0]])]});}
            var Q64;
            {var subQ0=sQuery(id+"F0.wireOp",EDGE,"E64");var subQ1=sQuery(id+"F0.wireOp",EDGE,"E0");var subQ2=makeQuery(id+"F0.imprint","INTERSECT",VERTEX,{"disambiguationData":[OD(0.0)],"derivedFrom":[subQ1,subQ0]});Q64=makeQuery(id+"F0.imprint","IMPRINT",FACE,{"disambiguationData":[TD([[makeQuery(id+"F0.imprint","IMPRINT",EDGE,{"disambiguationData":[TD([[subQ2,-1.0]])],"derivedFrom":subQ1}),1.0]])]});}
            var Q65;
            {var subQ0=sQuery(id+"F0.wireOp",EDGE,"E62");var subQ1=sQuery(id+"F0.wireOp",EDGE,"E0");var subQ2=makeQuery(id+"F0.imprint","INTERSECT",VERTEX,{"disambiguationData":[OD(0.0)],"derivedFrom":[subQ1,subQ0]});Q65=makeQuery(id+"F0.imprint","IMPRINT",FACE,{"disambiguationData":[TD([[makeQuery(id+"F0.imprint","IMPRINT",EDGE,{"disambiguationData":[TD([[subQ2,-1.0]])],"derivedFrom":subQ1}),-1.0]])]});}
            var Q66;
            {var subQ0=sQuery(id+"F0.wireOp",EDGE,"E63");var subQ1=sQuery(id+"F0.wireOp",EDGE,"E0");var subQ2=makeQuery(id+"F0.imprint","INTERSECT",VERTEX,{"disambiguationData":[OD(0.0)],"derivedFrom":[subQ1,subQ0]});Q66=makeQuery(id+"F0.imprint","IMPRINT",FACE,{"disambiguationData":[TD([[makeQuery(id+"F0.imprint","IMPRINT",EDGE,{"disambiguationData":[TD([[subQ2,-1.0]])],"derivedFrom":subQ1}),1.0]])]});}
            var Q67;
            {var subQ0=sQuery(id+"F0.wireOp",EDGE,"E63");var subQ1=sQuery(id+"F0.wireOp",EDGE,"E0");var subQ2=makeQuery(id+"F0.imprint","INTERSECT",VERTEX,{"disambiguationData":[OD(0.0)],"derivedFrom":[subQ1,subQ0]});Q67=makeQuery(id+"F0.imprint","IMPRINT",FACE,{"disambiguationData":[TD([[makeQuery(id+"F0.imprint","IMPRINT",EDGE,{"disambiguationData":[TD([[subQ2,-1.0]])],"derivedFrom":subQ1}),-1.0]])]});}
            var Q68;
            {var subQ0=sQuery(id+"F0.wireOp",EDGE,"E64");var subQ1=sQuery(id+"F0.wireOp",EDGE,"E0");var subQ2=makeQuery(id+"F0.imprint","INTERSECT",VERTEX,{"disambiguationData":[OD(0.0)],"derivedFrom":[subQ1,subQ0]});Q68=makeQuery(id+"F0.imprint","IMPRINT",FACE,{"disambiguationData":[TD([[makeQuery(id+"F0.imprint","IMPRINT",EDGE,{"disambiguationData":[TD([[subQ2,-1.0]])],"derivedFrom":subQ1}),-1.0]])]});}
            var Q69;
            {var subQ0=sQuery(id+"F0.wireOp",EDGE,"E3");var subQ1=sQuery(id+"F0.wireOp",EDGE,"E0");var subQ2=makeQuery(id+"F0.imprint","INTERSECT",VERTEX,{"derivedFrom":[subQ1,subQ0]});Q69=makeQuery(id+"F0.imprint","IMPRINT",FACE,{"disambiguationData":[TD([[makeQuery(id+"F0.imprint","IMPRINT",EDGE,{"disambiguationData":[TD([[subQ2,1.0]])],"derivedFrom":subQ1}),-1.0]])]});}
            var Q70;
            {var subQ0=sQuery(id+"F0.wireOp",EDGE,"E66");var subQ1=sQuery(id+"F0.wireOp",EDGE,"E59");var subQ2=makeQuery(id+"F0.imprint","INTERSECT",VERTEX,{"disambiguationData":[OD(0.0)],"derivedFrom":[subQ1,subQ0]});Q70=makeQuery(id+"F0.imprint","IMPRINT",FACE,{"disambiguationData":[TD([[makeQuery(id+"F0.imprint","IMPRINT",EDGE,{"disambiguationData":[TD([[subQ2,1.0]])],"derivedFrom":subQ1}),1.0]])]});}
            var Q71;
            {var subQ0=sQuery(id+"F0.wireOp",EDGE,"E67");var subQ1=sQuery(id+"F0.wireOp",EDGE,"E59");var subQ2=makeQuery(id+"F0.imprint","INTERSECT",VERTEX,{"disambiguationData":[OD(1.0)],"derivedFrom":[subQ1,subQ0]});Q71=makeQuery(id+"F0.imprint","IMPRINT",FACE,{"disambiguationData":[TD([[makeQuery(id+"F0.imprint","IMPRINT",EDGE,{"disambiguationData":[TD([[subQ2,-1.0]])],"derivedFrom":subQ1}),1.0]])]});}
            var Q72;
            {var subQ0=sQuery(id+"F0.wireOp",EDGE,"E3");var subQ1=sQuery(id+"F0.wireOp",EDGE,"E0");var subQ2=makeQuery(id+"F0.imprint","INTERSECT",VERTEX,{"derivedFrom":[subQ1,subQ0]});Q72=makeQuery(id+"F0.imprint","IMPRINT",FACE,{"disambiguationData":[TD([[makeQuery(id+"F0.imprint","IMPRINT",EDGE,{"disambiguationData":[TD([[subQ2,1.0]])],"derivedFrom":subQ1}),1.0]])]});}
            var Q73;
            {var subQ0=sQuery(id+"F0.wireOp",EDGE,"E68");var subQ1=sQuery(id+"F0.wireOp",EDGE,"E60");var subQ2=makeQuery(id+"F0.imprint","INTERSECT",VERTEX,{"disambiguationData":[OD(0.0)],"derivedFrom":[subQ1,subQ0]});Q73=makeQuery(id+"F0.imprint","IMPRINT",FACE,{"disambiguationData":[TD([[makeQuery(id+"F0.imprint","IMPRINT",EDGE,{"disambiguationData":[TD([[subQ2,1.0]])],"derivedFrom":subQ1}),1.0]])]});}
            var Q74;
            {var subQ3=sQuery(id+"F0.wireOp",EDGE,"E11");Q74=makeQuery(id+"F0.imprint","IMPRINT",FACE,{"disambiguationData":[TD([[makeQuery(id+"F0.imprint","IMPRINT",EDGE,{"derivedFrom":subQ3}),-1.0]])]});}
            var Q75;
            {var subQ3=sQuery(id+"F0.wireOp",EDGE,"E69");Q75=makeQuery(id+"F0.imprint","IMPRINT",FACE,{"disambiguationData":[TD([[makeQuery(id+"F0.imprint","IMPRINT",EDGE,{"derivedFrom":subQ3}),1.0]])]});}
            var Q76;
            {var subQ0=sQuery(id+"F0.wireOp",EDGE,"E67");var subQ1=sQuery(id+"F0.wireOp",EDGE,"E59");var subQ2=makeQuery(id+"F0.imprint","INTERSECT",VERTEX,{"disambiguationData":[OD(0.0)],"derivedFrom":[subQ1,subQ0]});Q76=makeQuery(id+"F0.imprint","IMPRINT",FACE,{"disambiguationData":[TD([[makeQuery(id+"F0.imprint","IMPRINT",EDGE,{"disambiguationData":[TD([[subQ2,1.0]])],"derivedFrom":subQ1}),1.0]])]});}
            var Q77;
            {var subQ0=sQuery(id+"F0.wireOp",EDGE,"E68");var subQ1=sQuery(id+"F0.wireOp",EDGE,"E60");var subQ2=makeQuery(id+"F0.imprint","INTERSECT",VERTEX,{"disambiguationData":[OD(1.0)],"derivedFrom":[subQ1,subQ0]});Q77=makeQuery(id+"F0.imprint","IMPRINT",FACE,{"disambiguationData":[TD([[makeQuery(id+"F0.imprint","IMPRINT",EDGE,{"disambiguationData":[TD([[subQ2,-1.0]])],"derivedFrom":subQ1}),1.0]])]});}
            var Q78;
            {var subQ0=sQuery(id+"F0.wireOp",EDGE,"E66");var subQ1=sQuery(id+"F0.wireOp",EDGE,"E60");var subQ2=makeQuery(id+"F0.imprint","INTERSECT",VERTEX,{"disambiguationData":[OD(0.0)],"derivedFrom":[subQ1,subQ0]});Q78=makeQuery(id+"F0.imprint","IMPRINT",FACE,{"disambiguationData":[TD([[makeQuery(id+"F0.imprint","IMPRINT",EDGE,{"disambiguationData":[TD([[subQ2,1.0]])],"derivedFrom":subQ1}),1.0]])]});}
            var Q79;
            {var subQ0=sQuery(id+"F0.wireOp",EDGE,"E9.MirrorCS");Q79=makeQuery(id+"F0.imprint","IMPRINT",FACE,{"disambiguationData":[TD([[makeQuery(id+"F0.imprint","IMPRINT",EDGE,{"derivedFrom":subQ0}),1.0]])]});}
            extrude(context, id + "F1", {"entities" : qUnion([Q0, Q1, Q2, Q3, Q4, Q5, Q6, Q7, Q8, Q9, Q10, Q11, Q12, Q13, Q14, Q15, Q16, Q17, Q18, Q19, Q20, Q21, Q22, Q23, Q24, Q25, Q26, Q27, Q28, Q29, Q30, Q31, Q32, Q33, Q34, Q35, Q36, Q37, Q38, Q39, Q40, Q41, Q42, Q43, Q44, Q45, Q46, Q47, Q48, Q49, Q50, Q51, Q52, Q53, Q54, Q55, Q56, Q57, Q58, Q59, Q60, Q61, Q62, Q63, Q64, Q65, Q66, Q67, Q68, Q69, Q70, Q71, Q72, Q73, Q74, Q75, Q76, Q77, Q78, Q79]), "oppositeDirection" : true, "depth" : 5.08 * mm});
        }
    });
